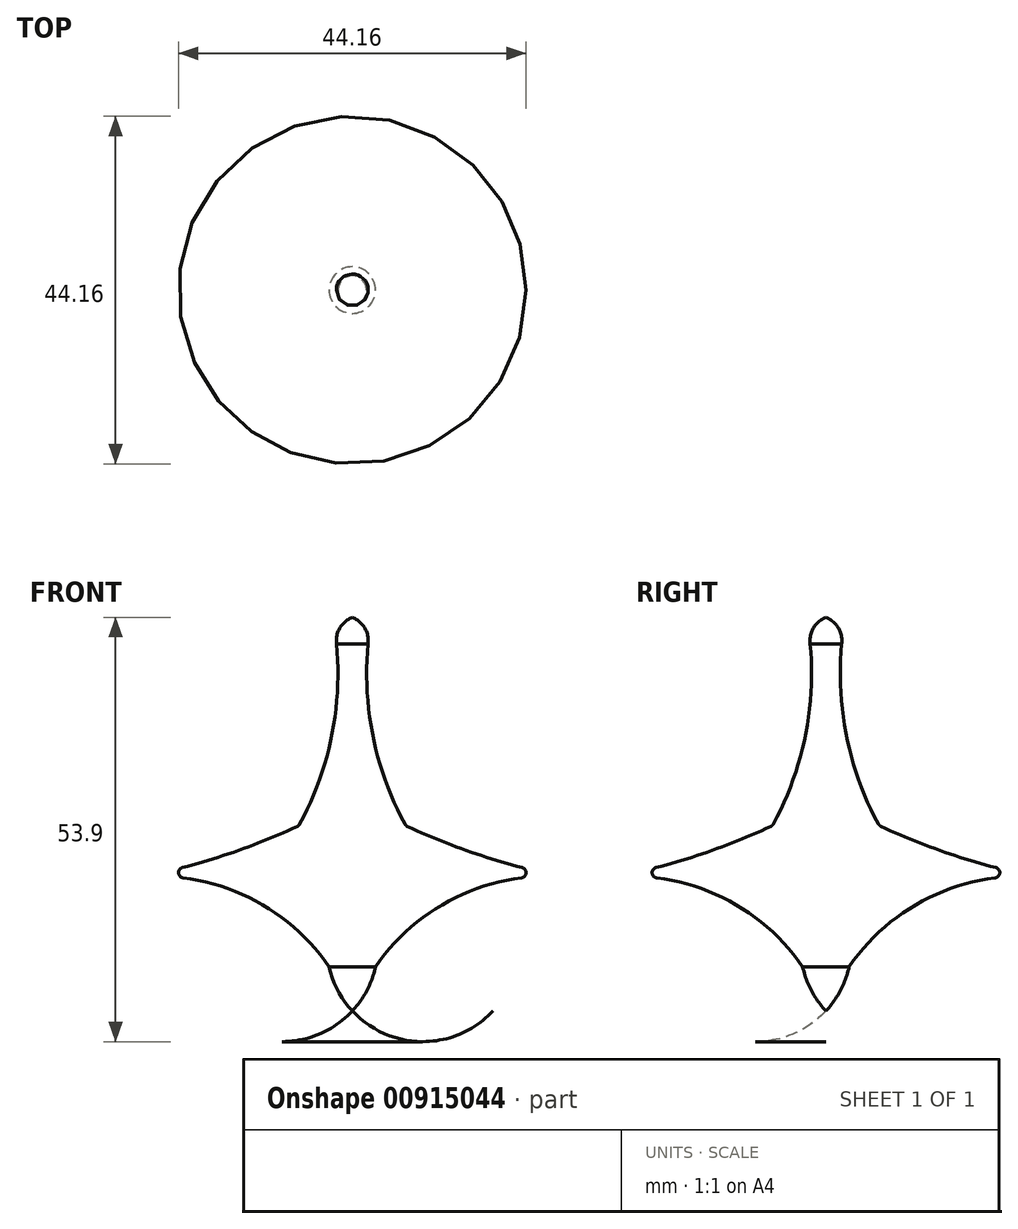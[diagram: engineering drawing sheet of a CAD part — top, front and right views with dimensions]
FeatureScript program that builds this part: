
annotation { "Feature Type Name" : "Feature", "Feature Type Description" : "" }
export const myFeature = defineFeature(function(context is Context, id is Id, definition is map)
    precondition{}
    {
        {
            var Q0;
            Q0=qCreatedBy(makeId("Front.planeOp"),FACE);
            var sketch = newSketch(context, id + "F0", { "sketchPlane" : qUnion([Q0])});
            skArc(sketch, "E0", {"start": v(-2.96, -11.42) * mm, "mid": v(-13.38, -2.5) * mm, "end": v(-26.87, 0) * mm});
            skArc(sketch, "E1", {"start": v(-26.87, 0) * mm, "mid": v(-16.62, 2.64) * mm, "end": v(-6.77, 6.52) * mm});
            skArc(sketch, "E2", {"start": v(-2.96, -11.42) * mm, "mid": v(-1.85, -14.42) * mm, "end": v(0, -17.03) * mm});
            skArc(sketch, "E3", {"start": v(-6.77, 6.52) * mm, "mid": v(-2.66, 17.7) * mm, "end": v(-2, 29.59) * mm});
            skArc(sketch, "E4", {"start": v(0, 32.97) * mm, "mid": v(-1.58, 31.62) * mm, "end": v(-2, 29.59) * mm});
            skLineSegment(sketch, "E5", {"start": v(0, 32.97) * mm, "end": v(0, -17.03) * mm});
            skSolve(sketch);
        }
        {
            var Q0;
            Q0=makeQuery(id+"F0.imprint","IMPRINT",FACE,{"disambiguationData":[TD([[makeQuery(id+"F0.imprint","IMPRINT",EDGE,{"derivedFrom":sQuery(id+"F0.wireOp",EDGE,"E0")}),-1.0]])]});
            var Q1;
            Q1=sQuery(id+"F0.wireOp",EDGE,"E5");
            revolve(context, id + "F1", {"surfaceOperationType" : NewSurfaceOperationType.NEW, "entities" : qUnion([Q0]), "axis" : qUnion([Q1]), "revolveType" : RevolveType.FULL});
        }
        {
            var Q0;
            Q0=makeQuery(id+"F1.opRevolve","SWEPT_FACE",FACE,{"disambiguationData":[OSD([sQuery(id+"F0.wireOp",EDGE,"E1")])]});
            fillet(context, id + "F2", {"entities" : qUnion([Q0]), "radius" : 0.67 * mm, "tangentPropagation" : true, "allowEdgeOverflow" : false});
        }
    });
